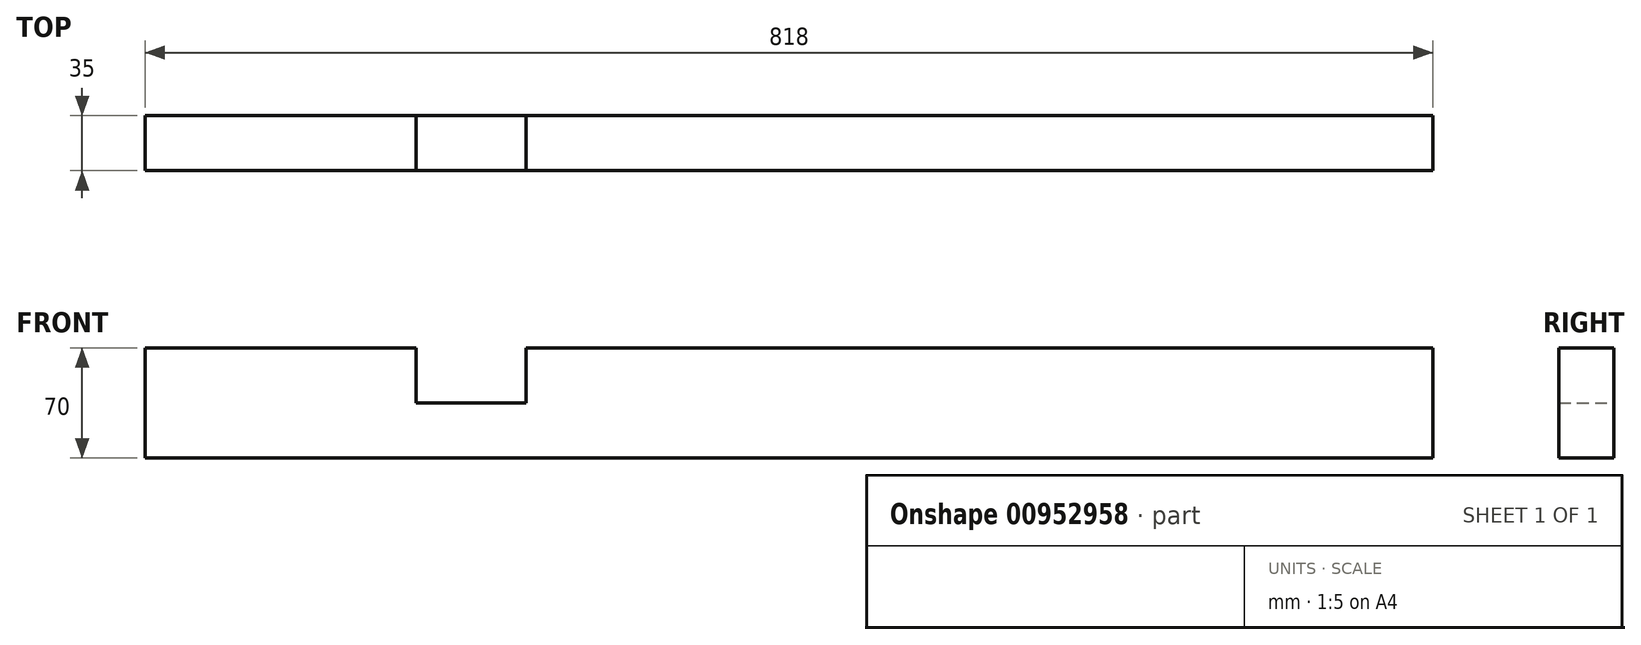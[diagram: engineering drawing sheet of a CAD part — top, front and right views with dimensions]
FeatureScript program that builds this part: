
annotation { "Feature Type Name" : "Feature", "Feature Type Description" : "" }
export const myFeature = defineFeature(function(context is Context, id is Id, definition is map)
    precondition{}
    {
        {
            var Q0;
            Q0=qCreatedBy(makeId("Front.planeOp"),FACE);
            var sketch = newSketch(context, id + "F0", { "sketchPlane" : qUnion([Q0])});
            skLineSegment(sketch, "E0.bottom", {"start": v(-406.34, -146.43) * mm, "end": v(411.66, -146.43) * mm});
            skLineSegment(sketch, "E0.top", {"start": v(-406.34, -216.43) * mm, "end": v(411.66, -216.43) * mm});
            skLineSegment(sketch, "E0.left", {"start": v(-406.34, -146.43) * mm, "end": v(-406.34, -216.43) * mm});
            skLineSegment(sketch, "E0.right", {"start": v(411.66, -146.43) * mm, "end": v(411.66, -216.43) * mm});
            skSolve(sketch);
        }
        {
            var Q0;
            Q0=makeQuery(id+"F0.imprint","IMPRINT",FACE,{"disambiguationData":[TD([[makeQuery(id+"F0.imprint","IMPRINT",EDGE,{"derivedFrom":sQuery(id+"F0.wireOp",EDGE,"E0.bottom")}),-1.0]])]});
            extrude(context, id + "F1", {"entities" : qUnion([Q0]), "oppositeDirection" : true, "depth" : 35 * mm, "offsetDistance" : 25 * mm});
        }
        {
            var Q0;
            Q0=makeQuery(id+"F1.opExtrude","SWEPT_FACE",FACE,{"disambiguationData":[OSD([sQuery(id+"F0.wireOp",EDGE,"E0.bottom")])]});
            var sketch = newSketch(context, id + "F2", { "sketchPlane" : qUnion([Q0])});
            skLineSegment(sketch, "E1.bottom", {"start": v(-234.25, 0) * mm, "end": v(-164.25, 0) * mm});
            skLineSegment(sketch, "E1.top", {"start": v(-234.25, 35) * mm, "end": v(-164.25, 35) * mm});
            skLineSegment(sketch, "E1.left", {"start": v(-234.25, 0) * mm, "end": v(-234.25, 35) * mm});
            skLineSegment(sketch, "E1.right", {"start": v(-164.25, 0) * mm, "end": v(-164.25, 35) * mm});
            skSolve(sketch);
        }
        {
            var Q0;
            Q0=makeQuery(id+"F2.imprint","IMPRINT",FACE,{"disambiguationData":[TD([[makeQuery(id+"F2.imprint","IMPRINT",EDGE,{"derivedFrom":sQuery(id+"F2.wireOp",EDGE,"E1.bottom")}),1.0]])]});
            var Q1;
            Q1 = qSketchRegion(id + "F2", true);
            extrude(context, id + "F3", {"entities" : qUnion([Q0, Q1]), "operationType" : NewBodyOperationType.REMOVE, "oppositeDirection" : true, "depth" : 35 * mm, "offsetDistance" : 25 * mm});
        }
    });
